FREECAD ASSEMBLY — COMPONENT RECIPES ("scorpius_assembly")

This assembly document has 11 components, labeled P0..P10 below (a component is one placed body or linked part). 0 of them carry a construction recipe — the FreeCAD feature program that regenerates the part from scratch, quoted from this document or its linked companion documents; the rest are supplied as boundary geometry only. No exploded tour is included for this assembly.
COMPONENT P0 — geometry summary ("Body"; no construction recipe available for this part):
  bounding box: 68.2 x 60.1 x 60.1 mm
  tessellated surface: 612 triangles
  volume: 14950 mm^3 (6% of its bounding box)
COMPONENT P1 — geometry summary ("Body001"; no construction recipe available for this part):
  bounding box: 68.2 x 60.1 x 60.1 mm
  tessellated surface: 612 triangles
  volume: 14950 mm^3 (6% of its bounding box)
COMPONENT P2 — geometry summary ("Body002"; no construction recipe available for this part):
  bounding box: 68.2 x 60.1 x 60.1 mm
  tessellated surface: 612 triangles
  volume: 14950 mm^3 (6% of its bounding box)
COMPONENT P3 — geometry summary ("Body003"; no construction recipe available for this part):
  bounding box: 68.2 x 60.1 x 60.1 mm
  tessellated surface: 612 triangles
  volume: 14950 mm^3 (6% of its bounding box)
COMPONENT P4 — geometry summary ("Body004"; no construction recipe available for this part):
  bounding box: 68.2 x 60.1 x 60.1 mm
  tessellated surface: 612 triangles
  volume: 14950 mm^3 (6% of its bounding box)
COMPONENT P5 — geometry summary ("Body005"; no construction recipe available for this part):
  bounding box: 68.2 x 60.1 x 60.1 mm
  tessellated surface: 612 triangles
  volume: 14950 mm^3 (6% of its bounding box)
COMPONENT P6 — geometry summary ("Body006"; no construction recipe available for this part):
  bounding box: 66.2 x 62.1 x 59.4 mm
  tessellated surface: 612 triangles
  volume: 14950 mm^3 (6% of its bounding box)
COMPONENT P7 — geometry summary ("Body007"; no construction recipe available for this part):
  bounding box: 79.2 x 50.1 x 43.0 mm
  tessellated surface: 612 triangles
  volume: 14950 mm^3 (9% of its bounding box)
COMPONENT P8 — geometry summary ("Body008"; no construction recipe available for this part):
  bounding box: 90.3 x 34.5 x 26.0 mm
  tessellated surface: 612 triangles
  volume: 14950 mm^3 (18% of its bounding box)
COMPONENT P9 — geometry summary ("Body009"; no construction recipe available for this part):
  bounding box: 87.7 x 51.2 x 30.8 mm
  tessellated surface: 612 triangles
  volume: 14950 mm^3 (11% of its bounding box)
COMPONENT P10 — geometry summary ("rhombic-dodecahedron"; no construction recipe available for this part):
  bounding box: 73.5 x 73.5 x 73.5 mm
  tessellated surface: 24 triangles
  volume: 99204 mm^3 (25% of its bounding box)
  symmetry: 2-fold rotationally symmetric about the x axis; 4-fold rotationally symmetric about the y axis; 4-fold rotationally symmetric about the z axis; mirror-symmetric across its x mid-plane, y mid-plane, z mid-plane
PROVENANCE & LICENSES
A FreeCAD (.FCStd) document from a public repository crawl; recipes are the document's own serialized feature recipes (and, for linked parts, companion documents' recipes).
License: as declared in the source repository (recorded in the dataset sidecar).
